# Revit family: SMC-SSTL-DRS
name_source: partatom
category: Plumbing Fixtures
revit_build: Autodesk Revit MEP 2016 (Build: 20150220_1215(x64)
units: mm (PartAtom-declared; Revit-internal decimal feet)

## family parameters
Cut with Voids When Loaded = No
Host = Face
OmniClass Number = 23.65.00.00
OmniClass Title = Supply and Distribution of Liquids and Gases
Part Type = Normal
Room Calculation Point = No
Round Connector Dimension = Use Diameter
Shared = Yes

## types (1)
- SMC-SSTL-DRS
    Assembly Code = D2020
    CW Connection = No
    CWFU = 0
    Default Elevation = 0"
    Description = Surface Mounted Cabinet, Stainless Steel, Solid Door for ET71-2
    HW Connection = No
    HWFU = 0
    Manufacturer = Acorn
    Material = Default
    Model = SMC-SSTL-DRS
    Revised Date = 09/17/19
    Tempered Water Connection = No
    URL = http://www.acorneng.com
    Vent Connection = No
    WFU = 0
    Waste Connection = No

## geometry (parser evidence)
native form markers: Sweep x3
no freeform markers — native parametric forms only
